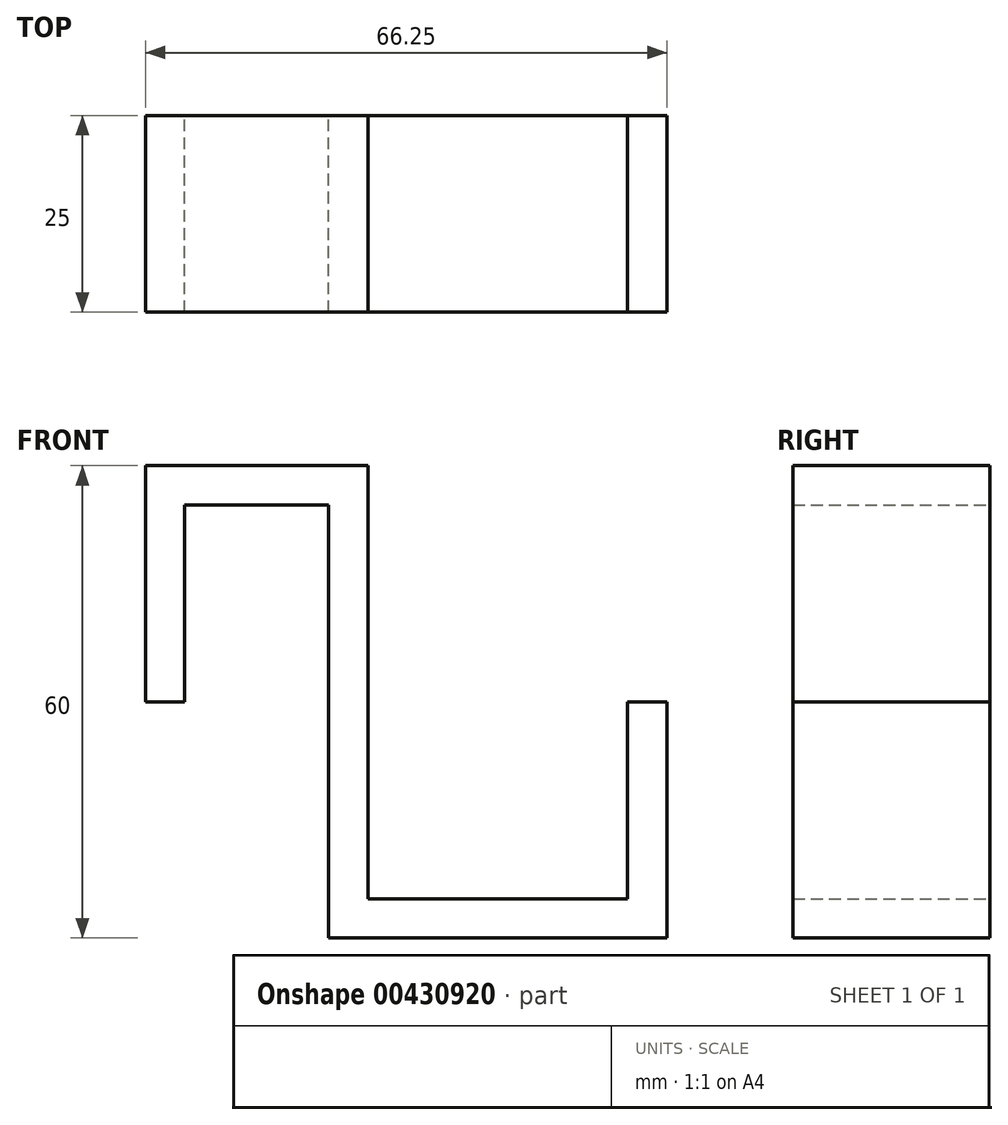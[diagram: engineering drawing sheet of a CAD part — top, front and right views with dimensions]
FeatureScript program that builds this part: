
annotation { "Feature Type Name" : "Feature", "Feature Type Description" : "" }
export const myFeature = defineFeature(function(context is Context, id is Id, definition is map)
    precondition{}
    {
        {
            var Q0;
            Q0=qCreatedBy(makeId("Front.planeOp"),FACE);
            var sketch = newSketch(context, id + "F0", { "sketchPlane" : qUnion([Q0])});
            skLineSegment(sketch, "E0", {"start": v(-23.25, 60) * mm, "end": v(-23.25, 30) * mm});
            skLineSegment(sketch, "E1", {"start": v(-23.25, 30) * mm, "end": v(-18.25, 30) * mm});
            skLineSegment(sketch, "E2", {"start": v(-18.25, 30) * mm, "end": v(-18.25, 55) * mm});
            skLineSegment(sketch, "E3", {"start": v(-18.25, 55) * mm, "end": v(0, 55) * mm});
            skLineSegment(sketch, "E4", {"start": v(0, 55) * mm, "end": v(0, 0) * mm});
            skLineSegment(sketch, "E5", {"start": v(0, 0) * mm, "end": v(43, 0) * mm});
            skLineSegment(sketch, "E6", {"start": v(43, 0) * mm, "end": v(43, 30) * mm});
            skLineSegment(sketch, "E7", {"start": v(43, 30) * mm, "end": v(38, 30) * mm});
            skLineSegment(sketch, "E8", {"start": v(38, 30) * mm, "end": v(38, 5) * mm});
            skLineSegment(sketch, "E9", {"start": v(38, 5) * mm, "end": v(5, 5) * mm});
            skLineSegment(sketch, "E10", {"start": v(5, 5) * mm, "end": v(5, 60) * mm});
            skLineSegment(sketch, "E11", {"start": v(5, 60) * mm, "end": v(-23.25, 60) * mm});
            skPoint(sketch, "E12.visualSharp", {"position": v(0, 0) * mm});
            skLineSegment(sketch, "E12.filletArc", {"start": v(0, 0) * mm, "end": v(0, 0) * mm});
            skPoint(sketch, "E13.visualSharp", {"position": v(43, 0) * mm});
            skLineSegment(sketch, "E13.filletArc", {"start": v(43, 0) * mm, "end": v(43, 0) * mm});
            skPoint(sketch, "E14.visualSharp", {"position": v(38, 5) * mm});
            skLineSegment(sketch, "E14.filletArc", {"start": v(38, 5) * mm, "end": v(38, 5) * mm});
            skPoint(sketch, "E15.visualSharp", {"position": v(5, 5) * mm});
            skLineSegment(sketch, "E15.filletArc", {"start": v(5, 5) * mm, "end": v(5, 5) * mm});
            skPoint(sketch, "E16.visualSharp", {"position": v(38, 30) * mm});
            skLineSegment(sketch, "E16.filletArc", {"start": v(38, 30) * mm, "end": v(38, 30) * mm});
            skPoint(sketch, "E17.visualSharp", {"position": v(43, 30) * mm});
            skLineSegment(sketch, "E17.filletArc", {"start": v(43, 30) * mm, "end": v(43, 30) * mm});
            skSolve(sketch);
        }
        {
            var Q0;
            Q0=makeQuery(id+"F0.imprint","IMPRINT",FACE,{"disambiguationData":[TD([[makeQuery(id+"F0.imprint","IMPRINT",EDGE,{"derivedFrom":sQuery(id+"F0.wireOp",EDGE,"E0")}),1.0]])]});
            extrude(context, id + "F1", {"entities" : qUnion([Q0]), "endBound" : BoundingType.SYMMETRIC, "depth" : 25 * mm});
        }
    });
